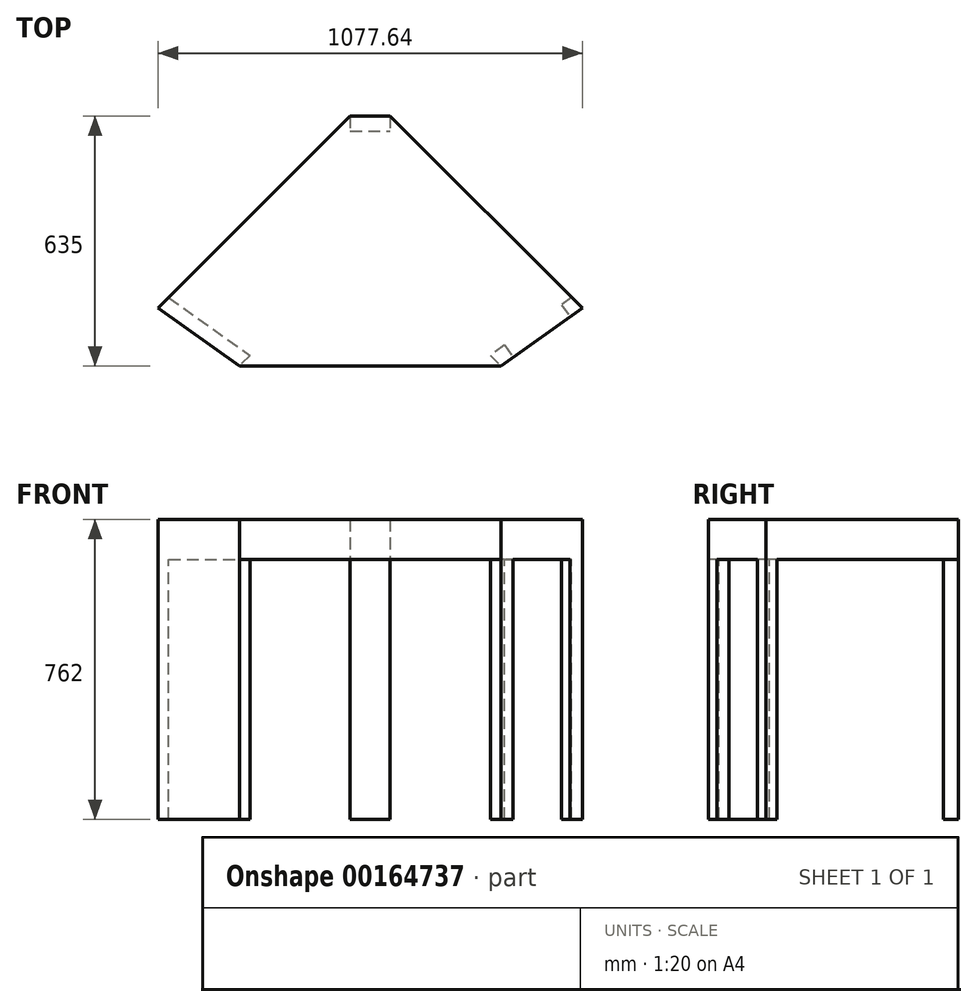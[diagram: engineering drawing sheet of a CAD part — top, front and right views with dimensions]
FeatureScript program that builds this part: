
annotation { "Feature Type Name" : "Feature", "Feature Type Description" : "" }
export const myFeature = defineFeature(function(context is Context, id is Id, definition is map)
    precondition{}
    {
        {
            var Q0;
            Q0=qCreatedBy(makeId("Top.planeOp"),FACE);
            var sketch = newSketch(context, id + "F0", { "sketchPlane" : qUnion([Q0])});
            skLineSegment(sketch, "E0.bottom", {"start": v(228.6, 228.6) * mm, "end": v(-228.6, 228.6) * mm});
            skLineSegment(sketch, "E0.top", {"start": v(228.6, -228.6) * mm, "end": v(-228.6, -228.6) * mm});
            skPoint(sketch, "E0.middle", {"position": v(0, 0) * mm});
            skPoint(sketch, "E1.endSnap0", {"position": v(0, 228.6) * mm});
            skLineSegment(sketch, "E2", {"start": v(-538.82, -81.62) * mm, "end": v(0, 457.2) * mm});
            skPoint(sketch, "E3.orphan", {"position": v(0, 578.03) * mm});
            skArc(sketch, "E4", {"start": v(-332.15, -228.6) * mm, "mid": v(0, -304.8) * mm, "end": v(332.15, -228.6) * mm});
            skLineSegment(sketch, "E5.MirrorCS", {"start": v(538.82, -81.62) * mm, "end": v(0, 457.2) * mm});
            skPoint(sketch, "E6.orphan", {"position": v(0, 406.4) * mm});
            skLineSegment(sketch, "E7", {"start": v(0, 457.2) * mm, "end": v(0, -203.2) * mm});
            skLineSegment(sketch, "E8", {"start": v(-50.8, 406.4) * mm, "end": v(50.8, 406.4) * mm});
            skLineSegment(sketch, "E9", {"start": v(-228.6, -228.6) * mm, "end": v(-332.15, -228.6) * mm});
            skLineSegment(sketch, "E10", {"start": v(-332.15, -228.6) * mm, "end": v(-332.15, 125.05) * mm});
            skLineSegment(sketch, "E11", {"start": v(228.6, -228.6) * mm, "end": v(332.15, -228.6) * mm});
            skLineSegment(sketch, "E12", {"start": v(332.15, -228.6) * mm, "end": v(332.15, 125.05) * mm});
            skLineSegment(sketch, "E13", {"start": v(-538.82, -81.62) * mm, "end": v(-332.15, -228.6) * mm});
            skLineSegment(sketch, "E14", {"start": v(332.15, -228.6) * mm, "end": v(538.82, -81.62) * mm});
            skSolve(sketch);
        }
        {
            var Q0;
            Q0=makeQuery(id+"F0.imprint","IMPRINT",FACE,{"disambiguationData":[TD([[makeQuery(id+"F0.imprint","IMPRINT",EDGE,{"derivedFrom":sQuery(id+"F0.wireOp",EDGE,"E0.top")}),-1.0]])]});
            var Q1;
            {var subQ0=sQuery(id+"F0.wireOp",EDGE,"E2");var subQ1=sQuery(id+"F0.wireOp",EDGE,"E0.bottom");var subQ2=makeQuery(id+"F0.imprint","INTERSECT",VERTEX,{"derivedFrom":[subQ1,subQ0]});Q1=makeQuery(id+"F0.imprint","IMPRINT",FACE,{"disambiguationData":[TD([[makeQuery(id+"F0.imprint","IMPRINT",EDGE,{"disambiguationData":[TD([[subQ2,1.0]])],"derivedFrom":subQ1}),-1.0]])]});}
            var Q2;
            {var subQ0=sQuery(id+"F0.wireOp",EDGE,"E5.MirrorCS");var subQ1=sQuery(id+"F0.wireOp",EDGE,"E0.bottom");var subQ2=makeQuery(id+"F0.imprint","INTERSECT",VERTEX,{"derivedFrom":[subQ1,subQ0]});Q2=makeQuery(id+"F0.imprint","IMPRINT",FACE,{"disambiguationData":[TD([[makeQuery(id+"F0.imprint","IMPRINT",EDGE,{"disambiguationData":[TD([[subQ2,-1.0]])],"derivedFrom":subQ1}),-1.0]])]});}
            var Q3;
            {var subQ3=sQuery(id+"F0.wireOp",EDGE,"E12");Q3=makeQuery(id+"F0.imprint","IMPRINT",FACE,{"disambiguationData":[TD([[makeQuery(id+"F0.imprint","IMPRINT",EDGE,{"derivedFrom":subQ3}),-1.0]])]});}
            var Q4;
            {var subQ3=sQuery(id+"F0.wireOp",EDGE,"E10");Q4=makeQuery(id+"F0.imprint","IMPRINT",FACE,{"disambiguationData":[TD([[makeQuery(id+"F0.imprint","IMPRINT",EDGE,{"derivedFrom":subQ3}),1.0]])]});}
            extrude(context, id + "F1", {"entities" : qUnion([Q0, Q1, Q2, Q3, Q4]), "depth" : 101.6 * mm});
        }
        {
            var Q0;
            Q0=makeQuery(id+"F1.opExtrude","CAP_FACE",FACE,{"disambiguationData":[OSD([sQuery(id+"F0.wireOp",EDGE,"E0.top"),sQuery(id+"F0.wireOp",EDGE,"E2"),sQuery(id+"F0.wireOp",EDGE,"E5.MirrorCS"),sQuery(id+"F0.wireOp",EDGE,"E8"),sQuery(id+"F0.wireOp",EDGE,"E9"),sQuery(id+"F0.wireOp",EDGE,"E11"),sQuery(id+"F0.wireOp",EDGE,"E13"),sQuery(id+"F0.wireOp",EDGE,"E14")])],"isStart":false});
            var sketch = newSketch(context, id + "F2", { "sketchPlane" : qUnion([Q0])});
            skLineSegment(sketch, "E15.left", {"start": v(-538.82, -81.62) * mm, "end": v(-538.82, -81.62) * mm});
            skLineSegment(sketch, "E15.right", {"start": v(-332.15, -228.6) * mm, "end": v(-332.15, -228.6) * mm});
            skPoint(sketch, "E16", {"position": v(-538.82, -81.62) * mm});
            skLineSegment(sketch, "E17", {"start": v(-538.82, -81.62) * mm, "end": v(-511.87, -54.67) * mm});
            skLineSegment(sketch, "E18", {"start": v(-511.87, -54.67) * mm, "end": v(-305.2, -201.66) * mm});
            skLineSegment(sketch, "E19", {"start": v(-305.2, -201.66) * mm, "end": v(-332.15, -228.6) * mm});
            skLineSegment(sketch, "E20.MirrorCS", {"start": v(511.87, -54.67) * mm, "end": v(305.2, -201.66) * mm});
            skLineSegment(sketch, "E21.MirrorCS", {"start": v(538.82, -81.62) * mm, "end": v(511.87, -54.67) * mm});
            skLineSegment(sketch, "E22.MirrorCS", {"start": v(305.2, -201.66) * mm, "end": v(332.15, -228.6) * mm});
            skLineSegment(sketch, "E23", {"start": v(-538.82, -81.62) * mm, "end": v(-332.15, -228.6) * mm});
            skLineSegment(sketch, "E24", {"start": v(332.15, -228.6) * mm, "end": v(538.82, -81.62) * mm});
            skLineSegment(sketch, "E25.bottom", {"start": v(-50.8, 406.4) * mm, "end": v(50.8, 406.4) * mm});
            skLineSegment(sketch, "E25.top", {"start": v(-50.8, 368.3) * mm, "end": v(50.8, 368.3) * mm});
            skLineSegment(sketch, "E25.left", {"start": v(-50.8, 406.4) * mm, "end": v(-50.8, 368.3) * mm});
            skLineSegment(sketch, "E25.right", {"start": v(50.8, 406.4) * mm, "end": v(50.8, 368.3) * mm});
            skSolve(sketch);
        }
        {
            var Q0;
            Q0=makeQuery(id+"F2.imprint","IMPRINT",FACE,{"disambiguationData":[TD([[makeQuery(id+"F2.imprint","IMPRINT",EDGE,{"derivedFrom":sQuery(id+"F2.wireOp",EDGE,"E17")}),-1.0]])]});
            var Q1;
            Q1=makeQuery(id+"F2.imprint","IMPRINT",FACE,{"disambiguationData":[TD([[makeQuery(id+"F2.imprint","IMPRINT",EDGE,{"derivedFrom":sQuery(id+"F2.wireOp",EDGE,"E20.MirrorCS")}),1.0]])]});
            var Q2;
            Q2=makeQuery(id+"F2.imprint","IMPRINT",FACE,{"disambiguationData":[TD([[makeQuery(id+"F2.imprint","IMPRINT",EDGE,{"derivedFrom":sQuery(id+"F2.wireOp",EDGE,"E25.bottom")}),-1.0]])]});
            extrude(context, id + "F3", {"entities" : qUnion([Q0, Q1, Q2]), "operationType" : NewBodyOperationType.ADD, "oppositeDirection" : true, "depth" : 762 * mm});
        }
        {
            var Q0;
            Q0=makeQuery(id+"F3.boolean.opBoolean","MERGE",FACE,{"derivedFrom":[makeQuery(id+"F1.opExtrude","SWEPT_FACE",FACE,{"disambiguationData":[OSD([sQuery(id+"F0.wireOp",EDGE,"E14")])]}),makeQuery(id+"F3.opExtrude","SWEPT_FACE",FACE,{"disambiguationData":[OSD([sQuery(id+"F2.wireOp",EDGE,"E24")])]})]});
            var sketch = newSketch(context, id + "F4", { "sketchPlane" : qUnion([Q0])});
            skLineSegment(sketch, "E26.bottom", {"start": v(176.28, 0) * mm, "end": v(353.69, 0) * mm});
            skLineSegment(sketch, "E26.top", {"start": v(176.28, -660.4) * mm, "end": v(353.69, -660.4) * mm});
            skLineSegment(sketch, "E26.left", {"start": v(176.28, 0) * mm, "end": v(176.28, -660.4) * mm});
            skLineSegment(sketch, "E26.right", {"start": v(353.69, 0) * mm, "end": v(353.69, -660.4) * mm});
            skSolve(sketch);
        }
        {
            var Q0;
            Q0=makeQuery(id+"F4.imprint","IMPRINT",FACE,{"disambiguationData":[TD([[makeQuery(id+"F4.imprint","IMPRINT",EDGE,{"derivedFrom":sQuery(id+"F4.wireOp",EDGE,"E26.bottom")}),-1.0]])]});
            extrude(context, id + "F5", {"entities" : qUnion([Q0]), "operationType" : NewBodyOperationType.REMOVE, "oppositeDirection" : true, "depth" : 76.2 * mm});
        }
    });
